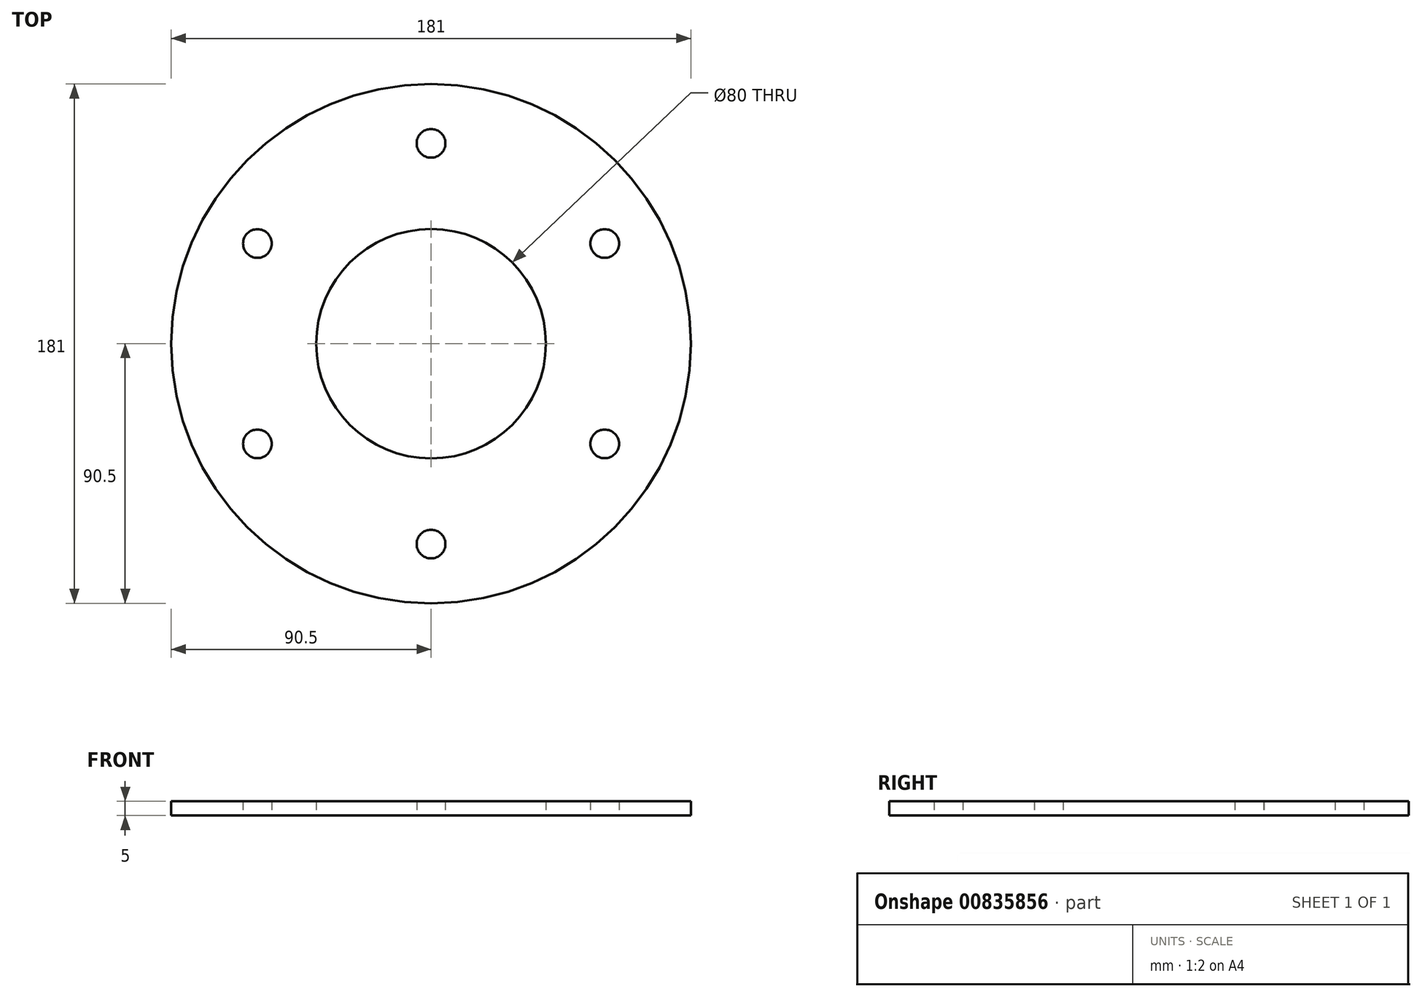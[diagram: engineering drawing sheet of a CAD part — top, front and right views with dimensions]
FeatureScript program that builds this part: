
annotation { "Feature Type Name" : "Feature", "Feature Type Description" : "" }
export const myFeature = defineFeature(function(context is Context, id is Id, definition is map)
    precondition{}
    {
        {
            var Q0;
            Q0=qCreatedBy(makeId("Top.planeOp"),FACE);
            var sketch = newSketch(context, id + "F0", { "sketchPlane" : qUnion([Q0])});
            skCircle(sketch, "E0", {"center": v(0, 0) * mm, "radius": 40 * mm});
            skCircle(sketch, "E1", {"center": v(0, 0) * mm, "radius": 90.5 * mm});
            skCircle(sketch, "E2", {"center": v(0, 0) * mm, "radius": 69.85 * mm, "construction": true});
            skLineSegment(sketch, "E3", {"start": v(0, 0) * mm, "end": v(0, 90.5) * mm, "construction": true});
            skLineSegment(sketch, "E4", {"start": v(0, 0) * mm, "end": v(78.38, 45.25) * mm, "construction": true});
            skLineSegment(sketch, "E5", {"start": v(0, 0) * mm, "end": v(78.38, -45.25) * mm, "construction": true});
            skLineSegment(sketch, "E6", {"start": v(0, 0) * mm, "end": v(0, -90.5) * mm, "construction": true});
            skLineSegment(sketch, "E7", {"start": v(0, 0) * mm, "end": v(-78.38, -45.25) * mm, "construction": true});
            skLineSegment(sketch, "E8", {"start": v(0, 0) * mm, "end": v(-78.38, 45.25) * mm, "construction": true});
            skCircle(sketch, "E9", {"center": v(0, 69.85) * mm, "radius": 5 * mm});
            skCircle(sketch, "E10", {"center": v(60.5, 34.93) * mm, "radius": 5 * mm});
            skCircle(sketch, "E11", {"center": v(60.5, -34.92) * mm, "radius": 5 * mm});
            skCircle(sketch, "E12", {"center": v(0, -69.85) * mm, "radius": 5 * mm});
            skCircle(sketch, "E13", {"center": v(-60.5, -34.93) * mm, "radius": 5 * mm});
            skCircle(sketch, "E14", {"center": v(-60.5, 34.92) * mm, "radius": 5 * mm});
            skSolve(sketch);
        }
        {
            var Q0;
            Q0 = qSketchRegion(id + "F0", true);
            extrude(context, id + "F1", {"entities" : qUnion([Q0]), "depth" : 5 * mm, "offsetDistance" : 25 * mm});
        }
    });
